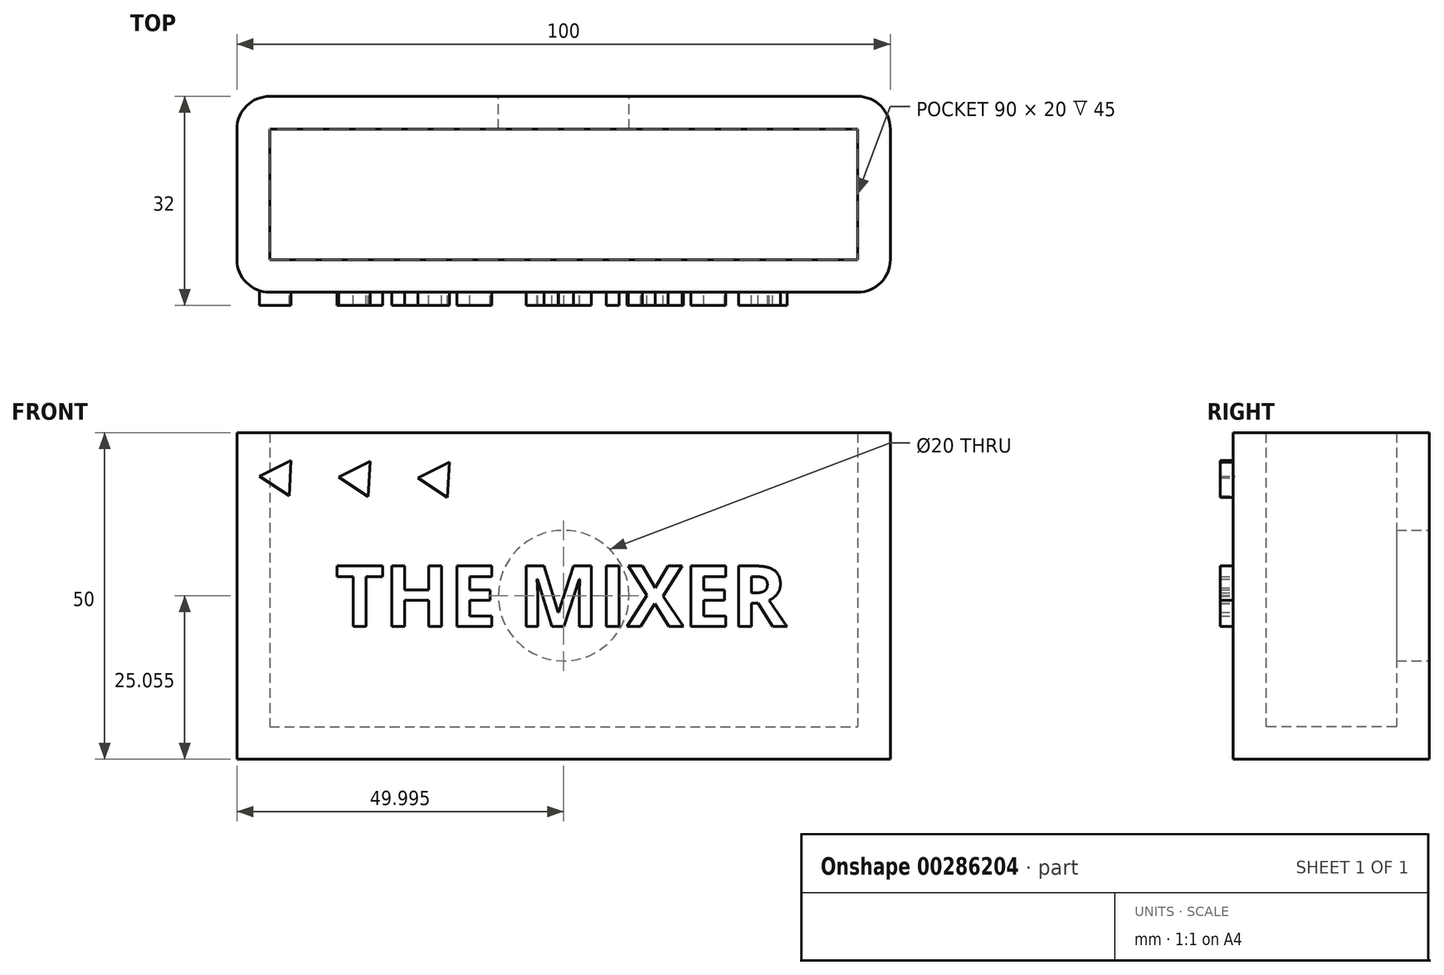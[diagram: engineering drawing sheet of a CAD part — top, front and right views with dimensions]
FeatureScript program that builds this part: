
annotation { "Feature Type Name" : "Feature", "Feature Type Description" : "" }
export const myFeature = defineFeature(function(context is Context, id is Id, definition is map)
    precondition{}
    {
        {
            var Q0;
            Q0=qCreatedBy(makeId("Top.planeOp"),FACE);
            var sketch = newSketch(context, id + "F0", { "sketchPlane" : qUnion([Q0])});
            skLineSegment(sketch, "E0.bottom", {"start": v(-46.06, 5.29) * mm, "end": v(53.94, 5.29) * mm});
            skLineSegment(sketch, "E0.top", {"start": v(-46.06, -24.71) * mm, "end": v(53.94, -24.71) * mm});
            skLineSegment(sketch, "E0.left", {"start": v(-46.06, 5.29) * mm, "end": v(-46.06, -24.71) * mm});
            skLineSegment(sketch, "E0.right", {"start": v(53.94, 5.29) * mm, "end": v(53.94, -24.71) * mm});
            skSolve(sketch);
        }
        {
            var Q0;
            Q0 = qSketchRegion(id + "F0", true);
            extrude(context, id + "F1", {"entities" : qUnion([Q0]), "depth" : 50 * mm});
        }
        {
            var Q0;
            Q0=makeQuery(id+"F1.opExtrude","CAP_FACE",FACE,{"disambiguationData":[OSD([sQuery(id+"F0.wireOp",EDGE,"E0.bottom"),sQuery(id+"F0.wireOp",EDGE,"E0.top"),sQuery(id+"F0.wireOp",EDGE,"E0.left"),sQuery(id+"F0.wireOp",EDGE,"E0.right")])],"isStart":false});
            shell(context, id + "F2", {"entities" : qUnion([Q0]), "thickness" : 5 * mm});
        }
        {
            var Q0;
            Q0=makeQuery(id+"F1.opExtrude","SWEPT_FACE",FACE,{"disambiguationData":[OSD([sQuery(id+"F0.wireOp",EDGE,"E0.top")])]});
            var sketch = newSketch(context, id + "F3", { "sketchPlane" : qUnion([Q0])});
            skText(sketch, "E1", { "text": "THE MIXER", "fontName": "OpenSans-Bold.ttf"});
            skLineSegment(sketch, "E2", {"start": v(38.96, 23.85) * mm, "end": v(53.94, 25) * mm, "construction": true});
            skLineSegment(sketch, "E3", {"start": v(-31.04, 25) * mm, "end": v(-46.06, 25) * mm, "construction": true});
            skLineSegment(sketch, "E4", {"start": v(3.96, 29.68) * mm, "end": v(3.96, 50) * mm, "construction": true});
            skLineSegment(sketch, "E5", {"start": v(3.96, 20.32) * mm, "end": v(3.96, 0) * mm, "construction": true});
            skLineSegment(sketch, "E6", {"start": v(-46.06, 43.14) * mm, "end": v(53.94, 43.14) * mm, "construction": true});
            skCircle(sketch, "E7.cCircle", {"center": v(-39.5, 43.14) * mm, "radius": 3.13 * mm, "construction": true});
            skLineSegment(sketch, "E7.0", {"start": v(-37.78, 45.76) * mm, "end": v(-38.09, 40.34) * mm});
            skLineSegment(sketch, "E7.1", {"start": v(-38.09, 40.34) * mm, "end": v(-42.62, 43.32) * mm});
            skLineSegment(sketch, "E7.2", {"start": v(-42.62, 43.32) * mm, "end": v(-37.78, 45.76) * mm});
            skLineSegment(sketch, "E8.1.0.0", {"start": v(-25.66, 45.64) * mm, "end": v(-25.96, 40.22) * mm});
            skLineSegment(sketch, "E8.1.0.1", {"start": v(-25.96, 40.22) * mm, "end": v(-30.5, 43.2) * mm});
            skLineSegment(sketch, "E8.1.0.2", {"start": v(-30.5, 43.2) * mm, "end": v(-25.66, 45.64) * mm});
            skLineSegment(sketch, "E8.2.0.0", {"start": v(-13.53, 45.52) * mm, "end": v(-13.84, 40.1) * mm});
            skLineSegment(sketch, "E8.2.0.1", {"start": v(-13.84, 40.1) * mm, "end": v(-18.38, 43.08) * mm});
            skLineSegment(sketch, "E8.2.0.2", {"start": v(-18.38, 43.08) * mm, "end": v(-13.53, 45.52) * mm});
            skLineSegment(sketch, "E8.direction1", {"start": v(-42.62, 43.32) * mm, "end": v(-30.5, 43.2) * mm, "construction": true});
            const initialGuessF3  = {"E1": [-0.03104, 0.02032, 1, 0, 0.00935]};
            skSetInitialGuess(sketch, initialGuessF3);
            skSolve(sketch);
        }
        {
            var Q0;
            Q0 = qSketchRegion(id + "F3", true);
            extrude(context, id + "F4", {"entities" : qUnion([Q0]), "operationType" : NewBodyOperationType.ADD, "depth" : 2 * mm});
        }
        {
            var Q0;
            Q0=makeQuery(id+"F1.opExtrude","SWEPT_EDGE",EDGE,{"disambiguationData":[OSD([sQuery(id+"F0.wireOp",EDGE,"E0.top"),sQuery(id+"F0.wireOp",EDGE,"E0.right")])]});
            var Q1;
            Q1=makeQuery(id+"F1.opExtrude","SWEPT_EDGE",EDGE,{"disambiguationData":[OSD([sQuery(id+"F0.wireOp",EDGE,"E0.bottom"),sQuery(id+"F0.wireOp",EDGE,"E0.right")])]});
            var Q2;
            Q2=makeQuery(id+"F1.opExtrude","SWEPT_EDGE",EDGE,{"disambiguationData":[OSD([sQuery(id+"F0.wireOp",EDGE,"E0.top"),sQuery(id+"F0.wireOp",EDGE,"E0.left")])]});
            var Q3;
            Q3=makeQuery(id+"F1.opExtrude","SWEPT_EDGE",EDGE,{"disambiguationData":[OSD([sQuery(id+"F0.wireOp",EDGE,"E0.bottom"),sQuery(id+"F0.wireOp",EDGE,"E0.left")])]});
            fillet(context, id + "F5", {"entities" : qUnion([Q0, Q1, Q2, Q3]), "radius" : 5 * mm, "tangentPropagation" : true, "allowEdgeOverflow" : false});
        }
        {
            var Q0;
            Q0=makeQuery(id+"F1.opExtrude","SWEPT_FACE",FACE,{"disambiguationData":[OSD([sQuery(id+"F0.wireOp",EDGE,"E0.bottom")])]});
            var sketch = newSketch(context, id + "F6", { "sketchPlane" : qUnion([Q0])});
            skCircle(sketch, "E9", {"center": v(-3.94, 25.05) * mm, "radius": 10 * mm});
            skLineSegment(sketch, "E10", {"start": v(-7.38, 50) * mm, "end": v(-7.38, 34.44) * mm, "construction": true});
            skLineSegment(sketch, "E11", {"start": v(-7.07, 15.56) * mm, "end": v(-7.07, 0) * mm, "construction": true});
            skLineSegment(sketch, "E12", {"start": v(-48.94, 25) * mm, "end": v(-13.93, 25) * mm, "construction": true});
            skLineSegment(sketch, "E13", {"start": v(6.06, 24.92) * mm, "end": v(41.06, 24.92) * mm, "construction": true});
            skSolve(sketch);
        }
        {
            var Q0;
            Q0=sQuery(id+"F6.wireOp",VERTEX,"E9.center");
            var Q1;
            Q1=makeQuery(id+"F1.opExtrude","SWEPT_BODY",BODY,{"disambiguationData":[OSD([sQuery(id+"F0.wireOp",EDGE,"E0.bottom"),sQuery(id+"F0.wireOp",EDGE,"E0.top"),sQuery(id+"F0.wireOp",EDGE,"E0.left"),sQuery(id+"F0.wireOp",EDGE,"E0.right")])]});
            hole(context, id + "F7", {"style" : HoleStyle.SIMPLE, "endStyle" : HoleEndStyle.BLIND, "holeDiameter" : 20 * mm, "holeDepth" : 12 * mm, "tappedDepth" : 12 * mm, "tapClearance" : 3, "locations" : qUnion([Q0]), "scope" : qUnion([Q1])});
        }
    });
